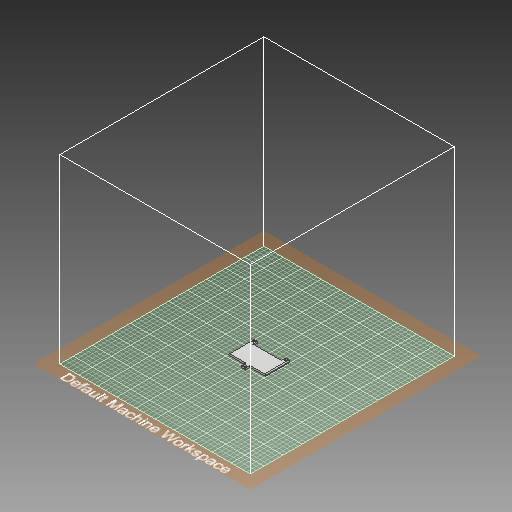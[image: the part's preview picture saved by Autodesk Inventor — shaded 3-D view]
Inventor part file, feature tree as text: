
AUTODESK INVENTOR PART (.ipt)
format: ipt  version: 2019.4 (Build 234330000, 330)  size: 364,032 bytes
history: native  units: in
note: dims shown in document units (in); Inventor stores cm internally (conversion verified against a paired STEP export)
features: sketch x4, extrude x3, fillet x1
ambient origin geometry x8: Origin, YZ Plane, XZ Plane, XY Plane, X Axis, Y Axis, Z Axis, Center Point
bodies: Solid1 (feature_tree)
feature tree (8):
  extrude  "Extrusion1"  Depth=1.7717in
  sketch  "Sketch2"  dims[d2=0.3937in d3=0.3937in]
  extrude  "Extrusion2"  Depth=0.3937in
  extrude  "Extrusion3"  Depth=0.3937in
  fillet  "Fillet2"  Radius=1.4878in
  sketch  "Sketch1"  dims[d0=3.2283in d1=1.7717in]
  sketch  "Sketch3"  dims[d4=0.3937in d5=0.3937in d10=1.4878in]
  sketch  "Sketch4"  dims[d11=0.3937in d12=0.3937in d15=0.126in d16=0.2362in d20=0.126in d21=0.126in d22=0.1575in d23=0.0in d24=0.2165in d25=0.2165in d26=0.2165in d27=0.0984in d28=0.0in d30=0.0197in d31=0.0197in d32=0.0197in d33=0.0197in d34=0.0197in d35=0.0197in d36=0.0197in d37=0.0197in d38=0.0197in d39=0.0197in d40=0.0197in d41=0.3937in d42=0.0in d43=0.0787in]
